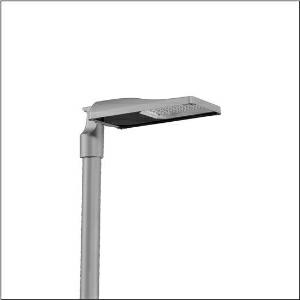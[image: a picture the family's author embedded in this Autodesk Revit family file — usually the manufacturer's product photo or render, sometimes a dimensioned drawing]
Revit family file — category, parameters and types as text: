
# Revit family: streetlight_sl_31_mini___st1_0a_5xh6d31a08ga_ae29
name_source: partatom
category: Lighting Fixtures
units: mm (PartAtom-declared; Revit-internal decimal feet)

## family parameters
Cut with Voids When Loaded = No
Host = Face
Light Source = No
Part Type = Normal
Room Calculation Point = No
Round Connector Dimension = Use Diameter
Shared = No

## types (1)
- --- (1 x LED, 5710 lm, 37.3 W, 3000K)
    Apparent Load = 37 VA
    CIE Flux Codes = 37 72 97 100 100
    Color Rendering = 70
    Color Temperature = 3000K
    Default Elevation = 1800 mm
    Description = Streetlight SL 31 mini Easy, Desk-Remote mast luminaire for post-top, side-entry; light control with lens of PMMA; light distribution: ST1.0a, direct asymmetric distribution, for standard-compliant lighting for roads and squares; LED: luminous flux: 5.710lm, light colour: 730, colour temperature: 3000K; luminous efficacy: 153,1lm/W; control: pre-setting: linear dimming characteristic, flexible luminous flux parameterisation, time-dependent luminous flux control, constant luminous flux control, intelligent temperature release in ECG and LED module, overheat protection; luminaire housing, of diecast aluminium, Siteco® metallic grey (DB 702S), corrosivity category C5 high according to DIN EN ISO 12944; cover of toughened safety glass, transparent, opened without tools; mast flange of diecast aluminium, Siteco® metallic grey (DB 702S), spigot size: 76/60mm, mast flange included unmounted; with cable H07RN-F 2x 1.5mm², cable length: 6,5m, connection cable pre-assembled; mains connection: 220..240V, AC, 50/60Hz; power consumption (at start of service life): 37,3W / (at end of service life): 38,7W / (with reduced operation 50%): 17,5W; protection rating (complete): IP66; insulation class (complete): insulation class II (safety insulation); impact resistance: IK10; certification: CE, ENEC, ENEC+, VDE, UKCA; permissible operating ambient temperature for outdoor applications: -40..+50°C; packaging unit: 1 piece

Light Distribution: ST1.0a
    Height = 76 mm
    Lamp = 1 x LED
    Lamp Light Flux = 5710 lm
    Lamp Power = 37.3 W
    Lamp count = 1
    Length = 547 mm
    Luminous efficacy = 153 lm/W
    Manufacturer = Siteco
    ModVariant = No
    Model = 5XH6D31A08GA
    Number of Poles = 1
    OnlyDefault = Yes
    Power Factor = 1
    Product Name = Streetlight SL 31 mini | ST1.0a
    Product group = mast luminaire | pylon top
    ProductGroupID = 6100
    Protection Class = Protection class II
    Protection Degree = IP 66
    RLX_Detail_Level = 1
    RLX_Emergency_Light_Flux = 0 lm
    RLX_Emergency_Type = 0
    RLX_Emergency_Type_DB = No
    RlxData = <blob elided: 39565 chars, md5=bded8697>
    Socket = socket
    Standby Power = 0 W
    System Light Flux = 5710 lm
    System Power = 37 W
    Type Comments = factory setting: luminous flux: 100 % | dim-lin: 254 | 386 mA
    Type Image = l_1300326.jpg
    URL = http://relux.com
    VarID = @adj_074779
    Voltage = 0 V
    Weight = 0.00 kg
    Width = 265 mm

## geometry (parser evidence)
native form markers: Blend x4, Sweep x9
no freeform markers — native parametric forms only
